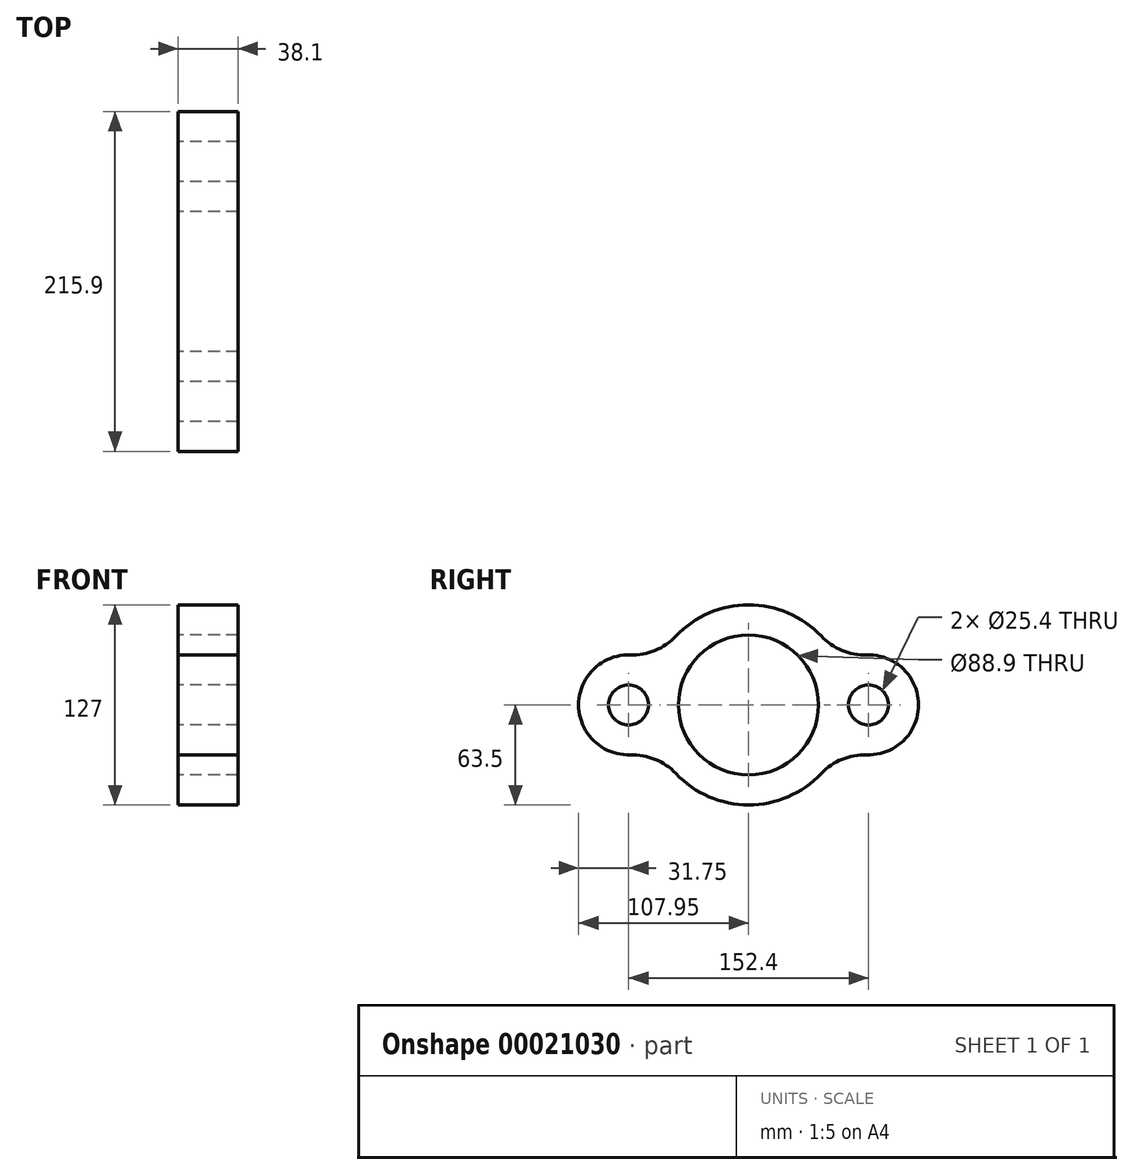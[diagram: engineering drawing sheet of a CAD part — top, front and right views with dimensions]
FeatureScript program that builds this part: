
annotation { "Feature Type Name" : "Feature", "Feature Type Description" : "" }
export const myFeature = defineFeature(function(context is Context, id is Id, definition is map)
    precondition{}
    {
        {
            var Q0;
            Q0=qCreatedBy(makeId("Right.planeOp"),FACE);
            var sketch = newSketch(context, id + "F0", { "sketchPlane" : qUnion([Q0])});
            skCircle(sketch, "E0", {"center": v(0, 0) * mm, "radius": 44.45 * mm});
            skCircle(sketch, "E1", {"center": v(-76.2, 0) * mm, "radius": 12.7 * mm});
            skCircle(sketch, "E2", {"center": v(76.2, 0) * mm, "radius": 12.7 * mm});
            skArc(sketch, "E3", {"start": v(-75.12, 31.73) * mm, "mid": v(-107.95, 0) * mm, "end": v(-75.12, -31.73) * mm});
            skArc(sketch, "E4", {"start": v(-46.14, -43.63) * mm, "mid": v(0, -63.5) * mm, "end": v(46.14, -43.63) * mm});
            skArc(sketch, "E5", {"start": v(75.12, -31.73) * mm, "mid": v(107.95, 0) * mm, "end": v(75.12, 31.73) * mm});
            skArc(sketch, "E6", {"start": v(-75.12, 31.73) * mm, "mid": v(-59.35, 34.56) * mm, "end": v(-46.14, 43.63) * mm});
            skArc(sketch, "E7", {"start": v(46.14, 43.63) * mm, "mid": v(59.35, 34.56) * mm, "end": v(75.12, 31.73) * mm});
            skArc(sketch, "E8", {"start": v(75.12, -31.73) * mm, "mid": v(59.35, -34.56) * mm, "end": v(46.14, -43.63) * mm});
            skArc(sketch, "E9", {"start": v(-46.14, -43.63) * mm, "mid": v(-59.35, -34.56) * mm, "end": v(-75.12, -31.73) * mm});
            skArc(sketch, "E10.trimOffspring", {"start": v(46.14, 43.63) * mm, "mid": v(0, 63.5) * mm, "end": v(-46.14, 43.63) * mm});
            skSolve(sketch);
        }
        {
            var Q0;
            Q0=makeQuery(id+"F0.imprint","IMPRINT",FACE,{"disambiguationData":[TD([[makeQuery(id+"F0.imprint","IMPRINT",EDGE,{"derivedFrom":sQuery(id+"F0.wireOp",EDGE,"E0")}),-1.0]])]});
            extrude(context, id + "F1", {"entities" : qUnion([Q0]), "depth" : 38.1 * mm});
        }
    });
